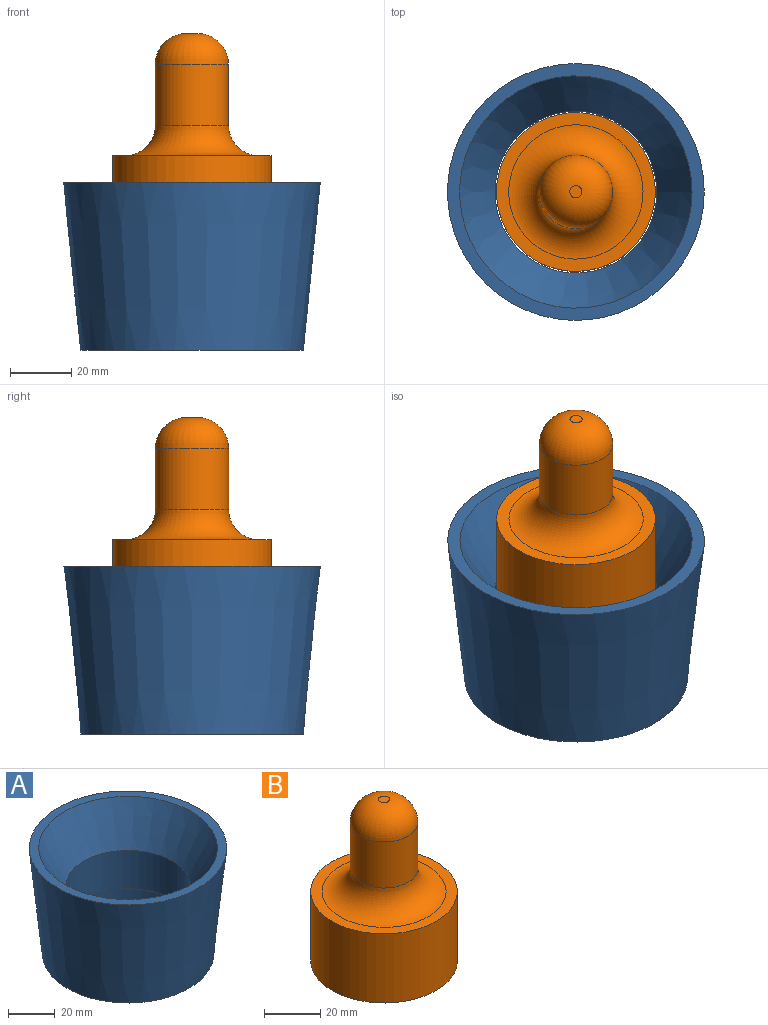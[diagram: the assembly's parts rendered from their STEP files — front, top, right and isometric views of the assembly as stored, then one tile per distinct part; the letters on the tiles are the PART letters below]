
ASSEMBLY  parts=2 mates=1
PART A: 7 faces, bbox 84.1x84.1x55 mm
  f0: cone r=38.05mm half-angle=30deg, axis (0,0,1), area 4683mm2, adj f1,f6
  f1: cylinder r=26.5mm len=53mm, axis (0,0,1), area 3330.1mm2, adj f0,f2
  f2: plane 65x65mm, normal (0,0,-1), area 1112.1mm2, adj f1,f3
  f3: cylinder r=32.5mm len=65mm, axis (0,0,1), area 3063.1mm2, adj f2,f4
  f4: plane 73x73mm, normal (0,0,-1), area 867.1mm2, adj f3,f5
  f5: cone r=36.5mm half-angle=5.8deg, axis (0,0,1), area 13640.8mm2, adj f4,f6
  f6: plane 84.09x84.09mm, normal (0,0,1), area 1006.5mm2, adj f0,f5
PART B: 7 faces, bbox 52x52x70 mm
  f0: cylinder r=12mm len=24mm, axis (0,0,1), area 1508mm2, adj f5,f6
  f1: plane 4x4mm, normal (0,0,1), area 12.6mm2, adj f5
  f2: plane 52x52mm, normal (0,0,-1), area 2123.7mm2, adj f3
  f3: cylinder r=26mm len=52mm, axis (0,0,1), area 4900.9mm2, adj f2,f4
  f4: plane 52x52mm, normal (0,0,1), area 603.2mm2, adj f3,f6
  f5: torus R=2mm, axis (0,0,-1), area 825.7mm2, adj f0,f1
  f6: torus R=22mm, axis (0,0,-1), area 1543mm2, adj f0,f4
PLACE A t=(-9.7,-0.51,-4.85)mm fixed
PLACE B rot(axis=(0,0,1),116.8deg) t=(-9.7,-0.51,13.87)mm
MATE cylindrical B.f0 <-> A.f0  axis (0,0,1) through (-9.7,-0.51,28.87)mm
